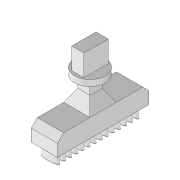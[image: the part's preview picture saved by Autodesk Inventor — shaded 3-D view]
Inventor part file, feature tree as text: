
AUTODESK INVENTOR PART (.ipt)
format: ipt  version: 2020 (Build 240168000, 168)  size: 634,880 bytes
history: native  units: mm
features: extrude x6, sketch x6, chamfer x1, fillet x1, projected_geometry x1
ambient origin geometry x8: Origin, YZ Plane, XZ Plane, XY Plane, X Axis, Y Axis, Z Axis, Center Point
bodies: Volumenkörper1 (feature_tree)
feature tree (15):
  extrude  "Extrusion1"  Depth=40.0mm
  extrude  "Extrusion2"  Depth=50.0mm
  extrude  "Extrusion3"  Depth=20.0mm
  extrude  "Extrusion4"  Depth=20.0mm TaperAngle=0.0deg
  extrude  "Extrusion5"  Depth=150.0mm
  chamfer  "Fase1"  Distance=30.0mm
  extrude  "Extrusion6"  Depth=10.0mm
  fillet  "Rundung1"  Radius=140.0mm
  sketch  "Skizze1"  dims[d0=20.0mm d1=40.0mm]
  sketch  "Skizze2"  dims[d2=35.0mm d3=0.0mm d4=50.0mm]
  sketch  "Skizze3"  dims[d5=10.0mm d6=0.0mm d7=20.0mm]
  sketch  "Skizze4"  dims[d8=20.0mm d9=20.0mm d10=0.0mm]
  projected_geometry  "Projizierte Kontur1"
  sketch  "Skizze5"  dims[d11=20.0mm d12=30.0deg d13=150.0mm d14=30.0mm d15=0.0mm]
  sketch  "Skizze6"  dims[d16=10.0mm d17=2.0mm d18=45.0deg d19=10.0mm d20=140.0mm d22=10.0mm d23=10.0mm d25=10.0mm d27=4.0mm d28=15.0mm d29=20.0mm d30=0.0mm d31=2.0mm]
